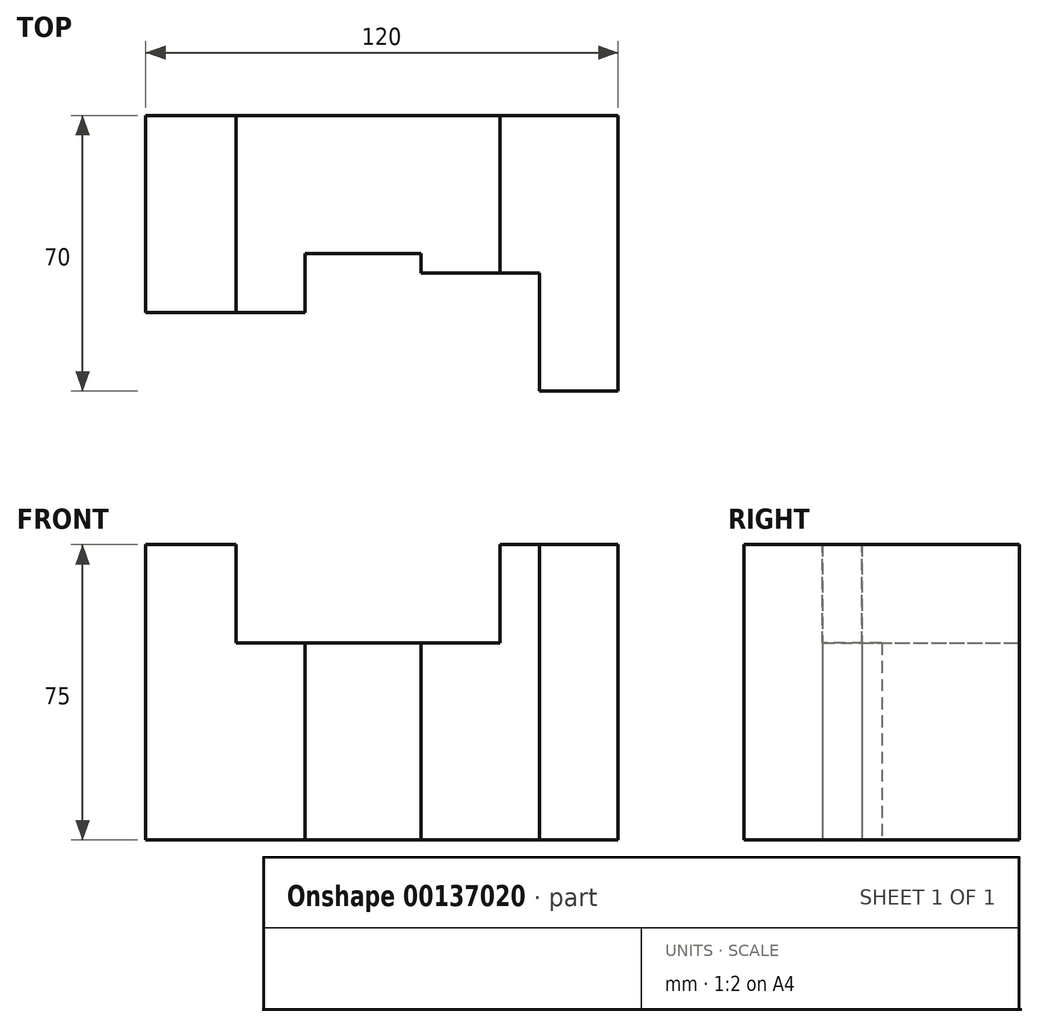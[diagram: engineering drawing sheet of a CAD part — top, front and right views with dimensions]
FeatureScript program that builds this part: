
annotation { "Feature Type Name" : "Feature", "Feature Type Description" : "" }
export const myFeature = defineFeature(function(context is Context, id is Id, definition is map)
    precondition{}
    {
        {
            var Q0;
            Q0=qCreatedBy(makeId("Top.planeOp"),FACE);
            var sketch = newSketch(context, id + "F0", { "sketchPlane" : qUnion([Q0])});
            skLineSegment(sketch, "E0", {"start": v(0, 0) * mm, "end": v(0, 50) * mm});
            skLineSegment(sketch, "E1", {"start": v(0, 50) * mm, "end": v(120, 50) * mm});
            skLineSegment(sketch, "E2", {"start": v(120, 50) * mm, "end": v(120, -20) * mm});
            skLineSegment(sketch, "E3", {"start": v(120, -20) * mm, "end": v(100, -20) * mm});
            skLineSegment(sketch, "E4", {"start": v(100, -20) * mm, "end": v(100, 10) * mm});
            skLineSegment(sketch, "E5", {"start": v(100, 10) * mm, "end": v(70, 10) * mm});
            skLineSegment(sketch, "E6", {"start": v(70, 10) * mm, "end": v(70, 15) * mm});
            skLineSegment(sketch, "E7", {"start": v(70, 15) * mm, "end": v(40.5, 15) * mm});
            skLineSegment(sketch, "E8", {"start": v(40.5, 15) * mm, "end": v(40.5, 0) * mm});
            skLineSegment(sketch, "E9", {"start": v(40.5, 0) * mm, "end": v(0, 0) * mm});
            skSolve(sketch);
        }
        {
            var Q0;
            Q0 = qSketchRegion(id + "F0", true);
            extrude(context, id + "F1", {"entities" : qUnion([Q0]), "depth" : 75 * mm});
        }
        {
            var Q0;
            Q0=makeQuery(id+"F1.opExtrude","CAP_FACE",FACE,{"disambiguationData":[OSD([sQuery(id+"F0.wireOp",EDGE,"E0"),sQuery(id+"F0.wireOp",EDGE,"E1"),sQuery(id+"F0.wireOp",EDGE,"E2"),sQuery(id+"F0.wireOp",EDGE,"E3"),sQuery(id+"F0.wireOp",EDGE,"E4"),sQuery(id+"F0.wireOp",EDGE,"E5"),sQuery(id+"F0.wireOp",EDGE,"E6"),sQuery(id+"F0.wireOp",EDGE,"E7"),sQuery(id+"F0.wireOp",EDGE,"E8"),sQuery(id+"F0.wireOp",EDGE,"E9")])],"isStart":false});
            var sketch = newSketch(context, id + "F2", { "sketchPlane" : qUnion([Q0])});
            skLineSegment(sketch, "E10", {"start": v(23, 0) * mm, "end": v(23, 50) * mm});
            skLineSegment(sketch, "E11", {"start": v(23, 0) * mm, "end": v(40.5, 0) * mm});
            skLineSegment(sketch, "E12", {"start": v(40.5, 0) * mm, "end": v(40.5, 15) * mm});
            skLineSegment(sketch, "E13", {"start": v(40.5, 15) * mm, "end": v(70, 15) * mm});
            skLineSegment(sketch, "E14", {"start": v(70, 15) * mm, "end": v(70, 10) * mm});
            skLineSegment(sketch, "E15", {"start": v(90, 10) * mm, "end": v(90, 50) * mm});
            skLineSegment(sketch, "E16", {"start": v(90, 50) * mm, "end": v(23, 50) * mm});
            skLineSegment(sketch, "E17", {"start": v(70, 10) * mm, "end": v(90, 10) * mm});
            skLineSegment(sketch, "E18", {"start": v(90, 10) * mm, "end": v(100, 10) * mm, "construction": true});
            skSolve(sketch);
        }
        {
            var Q0;
            Q0 = qSketchRegion(id + "F2", true);
            extrude(context, id + "F3", {"entities" : qUnion([Q0]), "operationType" : NewBodyOperationType.REMOVE, "oppositeDirection" : true, "depth" : 25 * mm});
        }
    });
